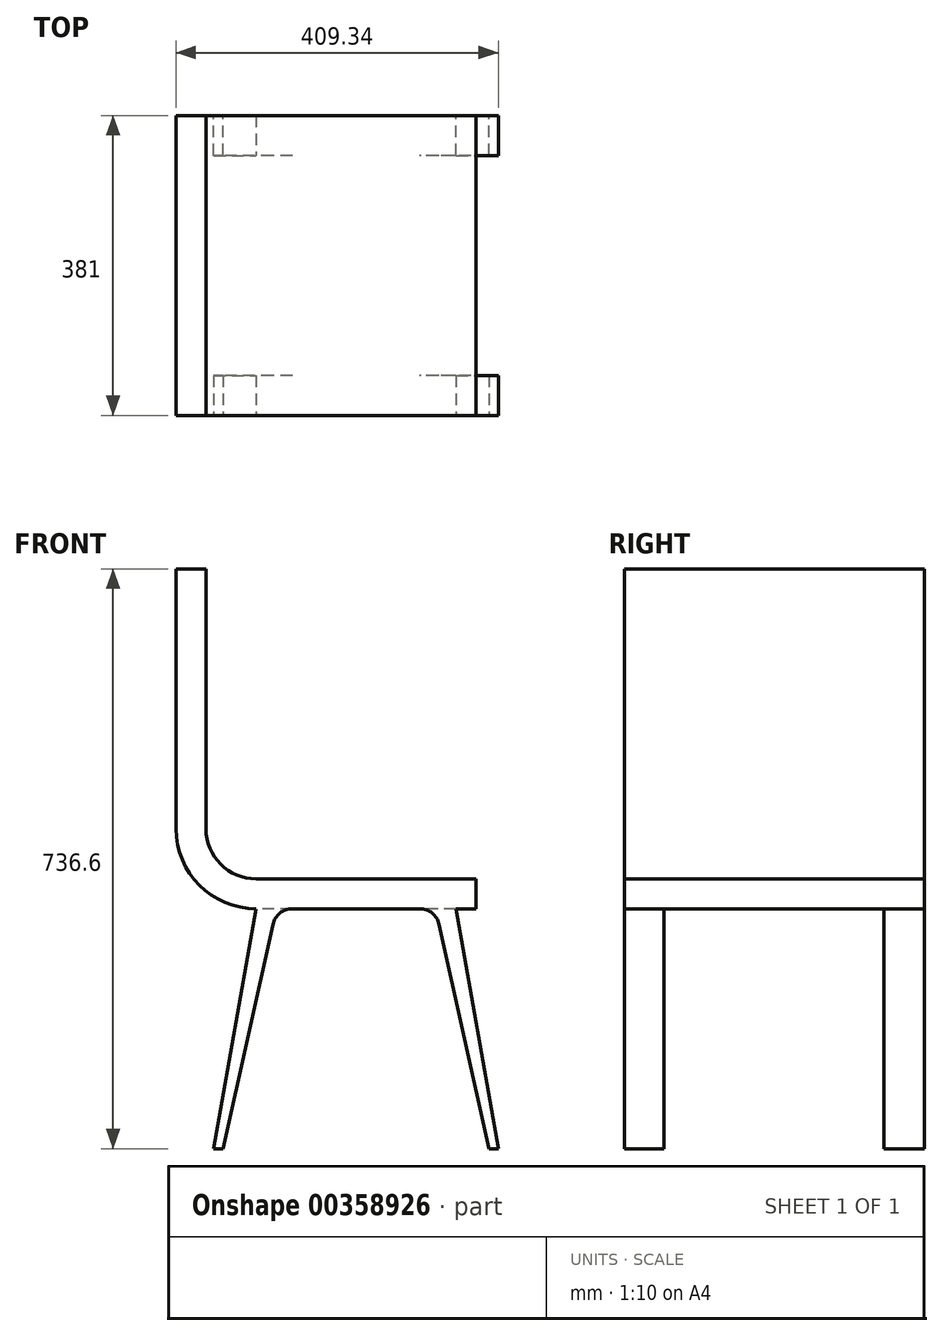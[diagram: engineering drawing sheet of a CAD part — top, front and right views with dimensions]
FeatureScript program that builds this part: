
annotation { "Feature Type Name" : "Feature", "Feature Type Description" : "" }
export const myFeature = defineFeature(function(context is Context, id is Id, definition is map)
    precondition{}
    {
        {
            var Q0;
            Q0=qCreatedBy(makeId("Front.planeOp"),FACE);
            var sketch = newSketch(context, id + "F0", { "sketchPlane" : qUnion([Q0])});
            skLineSegment(sketch, "E0", {"start": v(-381, 431.8) * mm, "end": v(-381, 101.6) * mm});
            skLineSegment(sketch, "E1", {"start": v(0, 0) * mm, "end": v(-279.4, 0) * mm});
            skPoint(sketch, "E2.visualSharp", {"position": v(-381, 0) * mm});
            skArc(sketch, "E2.filletArc", {"start": v(-381, 101.6) * mm, "mid": v(-351.24, 29.76) * mm, "end": v(-279.4, 0) * mm});
            skLineSegment(sketch, "E3.0", {"start": v(0, 38.1) * mm, "end": v(-279.4, 38.1) * mm});
            skArc(sketch, "E3.1", {"start": v(-342.9, 101.6) * mm, "mid": v(-324.3, 56.7) * mm, "end": v(-279.4, 38.1) * mm});
            skLineSegment(sketch, "E3.2", {"start": v(-342.9, 431.8) * mm, "end": v(-342.9, 101.6) * mm});
            skLineSegment(sketch, "E4", {"start": v(-342.9, 431.8) * mm, "end": v(-381, 431.8) * mm});
            skLineSegment(sketch, "E5", {"start": v(0, 0) * mm, "end": v(0, 38.1) * mm});
            skSolve(sketch);
        }
        {
            var Q0;
            Q0=makeQuery(id+"F0.imprint","IMPRINT",FACE,{"disambiguationData":[TD([[makeQuery(id+"F0.imprint","IMPRINT",EDGE,{"derivedFrom":sQuery(id+"F0.wireOp",EDGE,"E0")}),1.0]])]});
            extrude(context, id + "F1", {"entities" : qUnion([Q0]), "oppositeDirection" : true, "depth" : 381 * mm, "offsetDistance" : 25.4 * mm, "hasSecondDirection" : true, "secondDirectionOppositeDirection" : false, "secondDirectionDepth" : 25.4 * mm, "symmetric" : true});
        }
        {
            var Q0;
            Q0=makeQuery(id+"F1.opExtrude","CAP_FACE",FACE,{"disambiguationData":[OSD([sQuery(id+"F0.wireOp",EDGE,"E0"),sQuery(id+"F0.wireOp",EDGE,"E1"),sQuery(id+"F0.wireOp",EDGE,"E2.filletArc"),sQuery(id+"F0.wireOp",EDGE,"E3.0"),sQuery(id+"F0.wireOp",EDGE,"E3.1"),sQuery(id+"F0.wireOp",EDGE,"E3.2"),sQuery(id+"F0.wireOp",EDGE,"E4"),sQuery(id+"F0.wireOp",EDGE,"E5")])],"isStart":true});
            var sketch = newSketch(context, id + "F2", { "sketchPlane" : qUnion([Q0])});
            skLineSegment(sketch, "E6", {"start": v(-333.14, -304.8) * mm, "end": v(-279.4, 0) * mm});
            skLineSegment(sketch, "E7", {"start": v(-279.4, 0) * mm, "end": v(-25.4, 0) * mm});
            skLineSegment(sketch, "E8", {"start": v(-25.4, 0) * mm, "end": v(28.34, -304.8) * mm});
            skLineSegment(sketch, "E9", {"start": v(28.34, -304.8) * mm, "end": v(16.38, -304.8) * mm});
            skLineSegment(sketch, "E10", {"start": v(16.38, -304.8) * mm, "end": v(-46.78, -19.9) * mm});
            skLineSegment(sketch, "E11", {"start": v(-71.58, 0) * mm, "end": v(-233.22, 0) * mm});
            skLineSegment(sketch, "E12", {"start": v(-258.02, -19.9) * mm, "end": v(-321.18, -304.8) * mm});
            skLineSegment(sketch, "E13", {"start": v(-321.18, -304.8) * mm, "end": v(-333.14, -304.8) * mm});
            skPoint(sketch, "E14.visualSharp", {"position": v(-253.6, 0) * mm});
            skArc(sketch, "E14.filletArc", {"start": v(-233.22, 0) * mm, "mid": v(-249.12, -5.6) * mm, "end": v(-258.02, -19.9) * mm});
            skPoint(sketch, "E15.visualSharp", {"position": v(-51.2, 0) * mm});
            skArc(sketch, "E15.filletArc", {"start": v(-46.78, -19.9) * mm, "mid": v(-55.68, -5.6) * mm, "end": v(-71.58, 0) * mm});
            skSolve(sketch);
        }
        {
            var Q0;
            Q0=makeQuery(id+"F2.imprint","IMPRINT",FACE,{"disambiguationData":[TD([[makeQuery(id+"F2.imprint","IMPRINT",EDGE,{"derivedFrom":sQuery(id+"F2.wireOp",EDGE,"E6")}),-1.0]])]});
            var Q1;
            {var subQ0=sQuery(id+"F2.wireOp",EDGE,"E8");Q1=makeQuery(id+"F2.imprint","IMPRINT",FACE,{"disambiguationData":[TD([[makeQuery(id+"F2.imprint","IMPRINT",EDGE,{"derivedFrom":subQ0}),-1.0]])]});}
            extrude(context, id + "F3", {"entities" : qUnion([Q0, Q1]), "operationType" : NewBodyOperationType.ADD, "oppositeDirection" : true, "depth" : 50.8 * mm, "offsetDistance" : 25.4 * mm});
        }
        {
            var Q0;
            Q0=makeQuery(id+"F1.opExtrude","SWEPT_BODY",BODY,{"disambiguationData":[OSD([sQuery(id+"F0.wireOp",EDGE,"E0"),sQuery(id+"F0.wireOp",EDGE,"E1"),sQuery(id+"F0.wireOp",EDGE,"E2.filletArc"),sQuery(id+"F0.wireOp",EDGE,"E3.0"),sQuery(id+"F0.wireOp",EDGE,"E3.1"),sQuery(id+"F0.wireOp",EDGE,"E3.2"),sQuery(id+"F0.wireOp",EDGE,"E4"),sQuery(id+"F0.wireOp",EDGE,"E5")])]});
            var Q1;
            Q1=qCreatedBy(makeId("Front.planeOp"),FACE);
            mirror(context, id + "F4", {"operationType" : NewBodyOperationType.ADD, "entities" : qUnion([Q0]), "mirrorPlane" : qUnion([Q1])});
        }
    });
